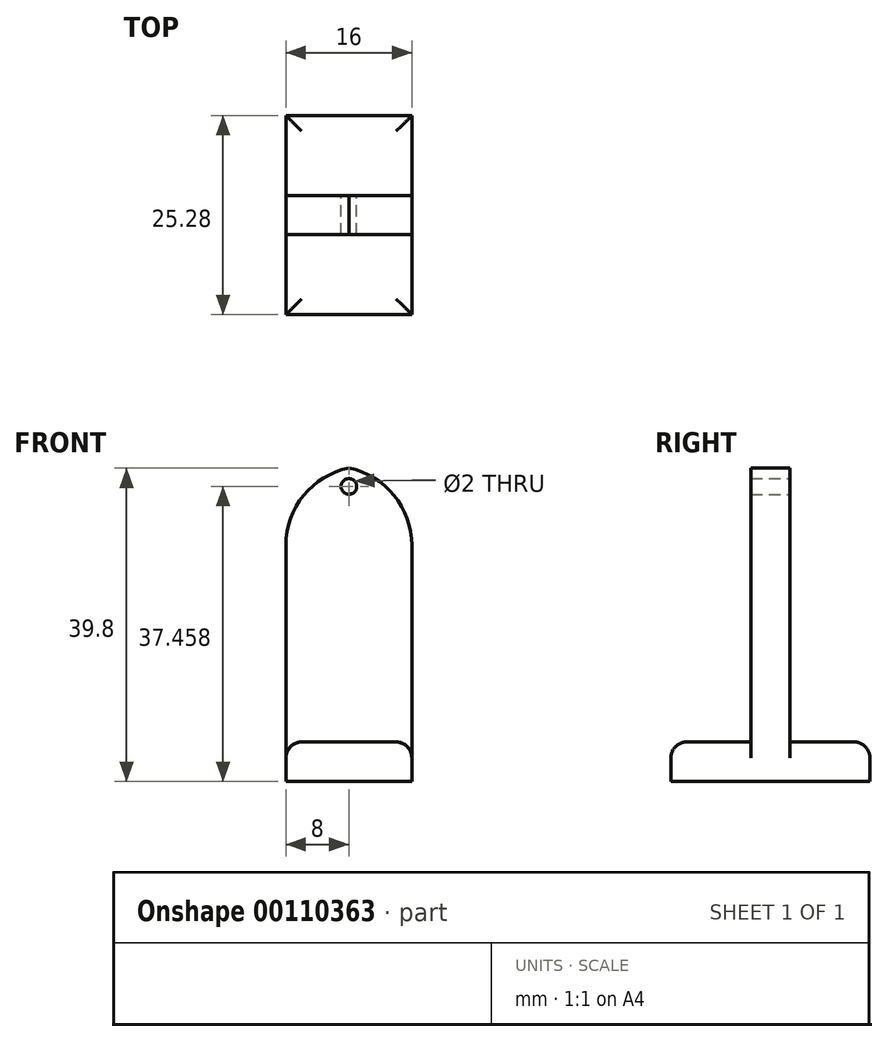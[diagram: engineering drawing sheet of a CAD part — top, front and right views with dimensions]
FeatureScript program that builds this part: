
annotation { "Feature Type Name" : "Feature", "Feature Type Description" : "" }
export const myFeature = defineFeature(function(context is Context, id is Id, definition is map)
    precondition{}
    {
        {
            var Q0;
            Q0=qCreatedBy(makeId("Top.planeOp"),FACE);
            var sketch = newSketch(context, id + "F0", { "sketchPlane" : qUnion([Q0])});
            skLineSegment(sketch, "E0.bottom", {"start": v(8, -2.5) * mm, "end": v(-8, -2.5) * mm});
            skLineSegment(sketch, "E0.top", {"start": v(8, 2.5) * mm, "end": v(-8, 2.5) * mm});
            skLineSegment(sketch, "E0.left", {"start": v(8, -2.5) * mm, "end": v(8, 2.5) * mm});
            skLineSegment(sketch, "E0.right", {"start": v(-8, -2.5) * mm, "end": v(-8, 2.5) * mm});
            skPoint(sketch, "E0.middle", {"position": v(0, 0) * mm});
            skSolve(sketch);
        }
        {
            var Q0;
            Q0 = qSketchRegion(id + "F0", true);
            extrude(context, id + "F1", {"entities" : qUnion([Q0]), "depth" : 35 * mm});
        }
        {
            var Q0;
            Q0=makeQuery(id+"F1.opExtrude","SWEPT_FACE",FACE,{"disambiguationData":[OSD([sQuery(id+"F0.wireOp",EDGE,"E0.top")])]});
            var sketch = newSketch(context, id + "F2", { "sketchPlane" : qUnion([Q0])});
            skCircle(sketch, "E1", {"center": v(0, 32.46) * mm, "radius": 1 * mm});
            skPoint(sketch, "E1.centerSnap0", {"position": v(0, 35) * mm});
            skSolve(sketch);
        }
        {
            var Q0;
            Q0 = qSketchRegion(id + "F2", true);
            extrude(context, id + "F3", {"entities" : qUnion([Q0]), "operationType" : NewBodyOperationType.REMOVE, "oppositeDirection" : true, "depth" : 5 * mm});
        }
        {
            var Q0;
            Q0=makeQuery(id+"F1.opExtrude","CAP_EDGE",EDGE,{"disambiguationData":[OSD([sQuery(id+"F0.wireOp",EDGE,"E0.right")])],"isStart":false});
            var Q1;
            Q1=makeQuery(id+"F1.opExtrude","CAP_EDGE",EDGE,{"disambiguationData":[OSD([sQuery(id+"F0.wireOp",EDGE,"E0.left")])],"isStart":false});
            fillet(context, id + "F4", {"entities" : qUnion([Q0, Q1]), "radius" : 10 * mm, "tangentPropagation" : true, "allowEdgeOverflow" : false});
        }
        {
            var Q0;
            Q0=qCreatedBy(makeId("Top.planeOp"),FACE);
            var sketch = newSketch(context, id + "F5", { "sketchPlane" : qUnion([Q0])});
            skLineSegment(sketch, "E2.bottom", {"start": v(8, -12.64) * mm, "end": v(-8, -12.64) * mm});
            skLineSegment(sketch, "E2.top", {"start": v(8, 12.64) * mm, "end": v(-8, 12.64) * mm});
            skLineSegment(sketch, "E2.left", {"start": v(8, -12.64) * mm, "end": v(8, 12.64) * mm});
            skLineSegment(sketch, "E2.right", {"start": v(-8, -12.64) * mm, "end": v(-8, 12.64) * mm});
            skPoint(sketch, "E2.middle", {"position": v(0, 0) * mm});
            skSolve(sketch);
        }
        {
            var Q0;
            Q0=makeQuery(id+"F5.imprint","IMPRINT",FACE,{"disambiguationData":[TD([[makeQuery(id+"F5.imprint","IMPRINT",EDGE,{"derivedFrom":sQuery(id+"F5.wireOp",EDGE,"E2.bottom")}),-1.0]])]});
            extrude(context, id + "F6", {"entities" : qUnion([Q0]), "operationType" : NewBodyOperationType.ADD, "oppositeDirection" : true, "depth" : 5 * mm});
        }
        {
            var Q0;
            {var subQ0=sQuery(id+"F5.wireOp",EDGE,"E2.left");Q0=makeQuery(id+"F6.boolean.opBoolean","SPLIT",EDGE,{"disambiguationData":[TD([makeQuery(id+"F1.opExtrude","SWEPT_FACE",FACE,{"disambiguationData":[OSD([sQuery(id+"F0.wireOp",EDGE,"E0.bottom")])]})])],"derivedFrom":makeQuery(id+"F6.opExtrude","CAP_EDGE",EDGE,{"disambiguationData":[OSD([subQ0])],"isStart":true})});}
            var Q1;
            {var subQ0=sQuery(id+"F5.wireOp",EDGE,"E2.left");Q1=makeQuery(id+"F6.boolean.opBoolean","SPLIT",EDGE,{"disambiguationData":[TD([makeQuery(id+"F1.opExtrude","SWEPT_FACE",FACE,{"disambiguationData":[OSD([sQuery(id+"F0.wireOp",EDGE,"E0.top")])]})])],"derivedFrom":makeQuery(id+"F6.opExtrude","CAP_EDGE",EDGE,{"disambiguationData":[OSD([subQ0])],"isStart":true})});}
            var Q2;
            Q2=makeQuery(id+"F6.opExtrude","CAP_EDGE",EDGE,{"disambiguationData":[OSD([sQuery(id+"F5.wireOp",EDGE,"E2.top")])],"isStart":true});
            var Q3;
            {var subQ0=sQuery(id+"F5.wireOp",EDGE,"E2.right");Q3=makeQuery(id+"F6.boolean.opBoolean","SPLIT",EDGE,{"disambiguationData":[TD([makeQuery(id+"F1.opExtrude","SWEPT_FACE",FACE,{"disambiguationData":[OSD([sQuery(id+"F0.wireOp",EDGE,"E0.top")])]})])],"derivedFrom":makeQuery(id+"F6.opExtrude","CAP_EDGE",EDGE,{"disambiguationData":[OSD([subQ0])],"isStart":true})});}
            var Q4;
            Q4=makeQuery(id+"F6.opExtrude","CAP_EDGE",EDGE,{"disambiguationData":[OSD([sQuery(id+"F5.wireOp",EDGE,"E2.bottom")])],"isStart":true});
            var Q5;
            {var subQ0=sQuery(id+"F5.wireOp",EDGE,"E2.right");Q5=makeQuery(id+"F6.boolean.opBoolean","SPLIT",EDGE,{"disambiguationData":[TD([makeQuery(id+"F1.opExtrude","SWEPT_FACE",FACE,{"disambiguationData":[OSD([sQuery(id+"F0.wireOp",EDGE,"E0.bottom")])]})])],"derivedFrom":makeQuery(id+"F6.opExtrude","CAP_EDGE",EDGE,{"disambiguationData":[OSD([subQ0])],"isStart":true})});}
            fillet(context, id + "F7", {"entities" : qUnion([Q0, Q1, Q2, Q3, Q4, Q5]), "radius" : 2 * mm, "tangentPropagation" : true, "allowEdgeOverflow" : false});
        }
    });
